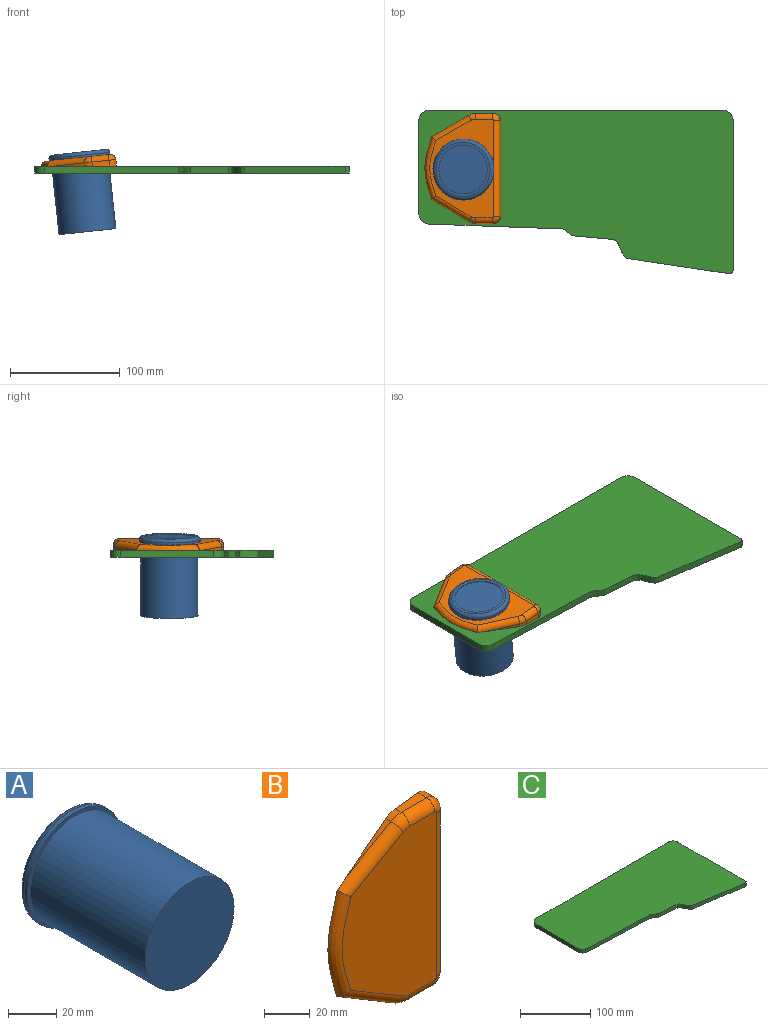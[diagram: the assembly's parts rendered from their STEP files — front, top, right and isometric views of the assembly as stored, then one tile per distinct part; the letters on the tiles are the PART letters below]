
ASSEMBLY  parts=3 mates=2
PART A: 8 faces, bbox 60.2x72.5x60.2 mm
  f0: cylinder r=26mm len=67.5mm, axis (0,1,0), area 11027mm2, adj f1,f4
  f1: plane 52x52mm, normal (0,-1,0), area 2123.7mm2, adj f0
  f2: cylinder r=27.8mm len=55.6mm, axis (0,-1,0), area 341mm2, adj f4,f5
  f3: plane 49.5x49.5mm, normal (0,1,0), area 383.4mm2, adj f5,f6
  f4: plane 55.6x55.6mm, normal (0,-1,0), area 304.2mm2, adj f0,f2
  f5: torus R=24.75mm, axis (0,1,0), area 803mm2, adj f2,f3
  f6: cylinder r=22.15mm len=44.3mm, axis (0,1,0), area 139.2mm2, adj f3,f7
  f7: plane 44.3x44.3mm, normal (0,1,0), area 1541.3mm2, adj f6
PART B: 21 faces, bbox 70x12.7x103.7 mm
  f0: plane 15.54x5.36mm, normal (0,0,-1), area 70.3mm2, adj f7,f8,f10,f13
  f1: plane 87.38x6.03mm, normal (1,0,0), area 527.1mm2, adj f2,f8,f10,f12
  f2: cylinder r=6.35mm len=6.35mm, axis (0,1,0), area 56.8mm2, adj f1,f3,f10,f14
  f3: plane 15.65x5.36mm, normal (0,0,1), area 70.7mm2, adj f2,f4,f10,f16
  f4: cylinder r=12.7mm len=6.35mm, axis (0,1,0), area 22.3mm2, adj f3,f5,f10,f18
  f5: plane 28.23x16.3mm, normal (-0.5,0,0.87), area 49.1mm2, adj f4,f10,f20
  f6: plane 28.17x16.86mm, normal (-0.51,0,-0.86), area 49.3mm2, adj f7,f10,f17
  f7: cylinder r=12.7mm len=6.52mm, axis (0,1,0), area 23mm2, adj f0,f6,f10,f15
  f8: cylinder r=6.35mm len=6.35mm, axis (0,1,0), area 56.8mm2, adj f0,f1,f10,f11
  f9: plane 89.92x58.49mm, normal (0,-1,0), area 4253mm2, adj f11,f12,f13,f14,f15,f16,f17,f18
  f10: plane 101.62x70.03mm, normal (-0.11,0.99,0), area 5665mm2, adj f0,f1,f2,f3,f4,f5,f6,f7
  f11: torus R=1.27mm, axis (0,-1,0), area 56.5mm2, adj f8,f9,f12,f13
  f12: cylinder r=5.08mm len=87.38mm, axis (0,0,-1), area 697.3mm2, adj f1,f9,f11,f14
  f13: cylinder r=5.08mm len=15.54mm, axis (-1,0,0), area 124mm2, adj f0,f9,f11,f15
  f14: torus R=1.27mm, axis (0,-1,0), area 56.5mm2, adj f2,f9,f12,f16
  f15: torus R=7.62mm, axis (0,-1,0), area 46.7mm2, adj f7,f9,f13,f17
  f16: cylinder r=5.08mm len=15.65mm, axis (1,0,0), area 124.9mm2, adj f3,f9,f14,f18
  f17: cylinder r=5.08mm len=36.55mm, axis (-0.86,0,0.51), area 306.7mm2, adj f6,f9,f10,f15,f19
  f18: torus R=7.62mm, axis (0,-1,0), area 45.3mm2, adj f4,f9,f16,f20
  f19: bspline ~59.4x11.56mm, area 382.6mm2, adj f9,f10,f17,f20
  f20: cylinder r=5.08mm len=36.37mm, axis (0.87,0,0.5), area 302.7mm2, adj f5,f9,f10,f18,f19
PART C: 14 faces, bbox 285.8x148.7x6.4 mm
  f0: plane 84.48x6.35mm, normal (-1,0,0), area 536.4mm2, adj f1,f11,f12,f13
  f1: cylinder r=9.53mm len=9.52mm, axis (0,0,-1), area 92.8mm2, adj f0,f2,f12,f13
  f2: plane 121x6.35mm, normal (-0.04,-1,0), area 768.9mm2, adj f1,f3,f12,f13
  f3: extruded ~11.11x6.35mm, area 82.4mm2, adj f2,f4,f12,f13
  f4: plane 34.93x6.35mm, normal (-0.09,-1,0), area 222.7mm2, adj f3,f5,f12,f13
  f5: extruded ~17.46x14.29mm, area 150.2mm2, adj f4,f6,f12,f13
  f6: plane 91.6x13.74mm, normal (-0.15,-0.99,0), area 588.2mm2, adj f5,f7,f12,f13
  f7: cylinder r=3.17mm len=6.35mm, axis (0,0,-1), area 34.7mm2, adj f6,f8,f12,f13
  f8: plane 136.01x6.35mm, normal (1,0,0), area 863.7mm2, adj f7,f9,f12,f13
  f9: cylinder r=9.53mm len=9.53mm, axis (0,0,-1), area 95mm2, adj f8,f10,f12,f13
  f10: plane 266.7x6.35mm, normal (0,1,0), area 1693.5mm2, adj f9,f11,f12,f13
  f11: cylinder r=9.53mm len=9.53mm, axis (0,0,-1), area 95mm2, adj f0,f10,f12,f13
  f12: plane 285.75x148.71mm, normal (0,0,1), area 34298.5mm2, adj f0,f1,f2,f3,f4,f5,f6,f7
  f13: plane 285.75x148.71mm, normal (0,0,-1), area 34298.5mm2, adj f0,f1,f2,f3,f4,f5,f6,f7
PLACE A rot(axis=(1,-0.05,0.05),90.2deg) t=(-64.16,164.13,128.53)mm
PLACE B rot(axis=(-1,-0.05,-0.05),90.2deg) t=(-60.78,165.08,117.72)mm
PLACE C t=(-104.82,114.9,114.59)mm
MATE planar A.f0 <-> B.f9  axis (0.11,0,-0.99) through (-64.16,164.13,128.53)mm
MATE planar B.f10 <-> C.f12  axis (0,0,-1) through (-60.6,165.18,120.94)mm
